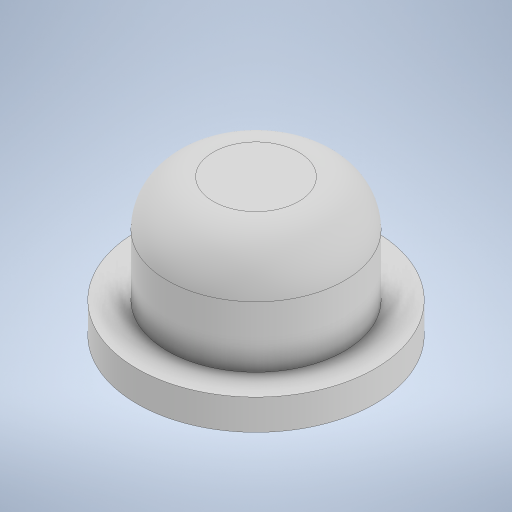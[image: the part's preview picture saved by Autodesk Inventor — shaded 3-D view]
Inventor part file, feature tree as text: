
AUTODESK INVENTOR PART (.ipt)
format: ipt  version: 2023 (Build 270158000, 158)  size: 251,392 bytes
history: native  units: in
note: dims shown in document units (in); Inventor stores cm internally (conversion verified against a paired STEP export)
features: extrude x2, sketch x1, fillet x1
ambient origin geometry x8: Origin, YZ Plane, XZ Plane, XY Plane, X Axis, Y Axis, Z Axis, Center Point
bodies: Solid1 (feature_tree)
feature tree (4):
  sketch  "Sketch1"  dims[d0=0.29in d1=0.39in d2=0.225in d3=0.0in d4=0.05in d5=0.0in d6=0.075in]
  extrude  "Extrusion1"  Depth=0.075in
  extrude  "Extrusion2"  Depth=0.225in TaperAngle=0.0deg
  fillet  "Fillet1"  Radius=0.05in
